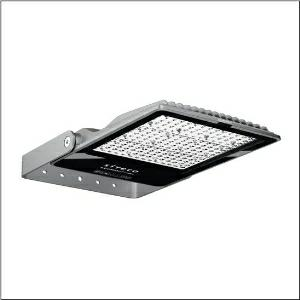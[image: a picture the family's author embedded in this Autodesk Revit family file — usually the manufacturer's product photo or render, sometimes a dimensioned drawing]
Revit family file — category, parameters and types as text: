
# Revit family: sicompact_r__31_midi___pl32_5xa7581e2k23_2195
name_source: partatom
category: Lighting Fixtures
units: mm (PartAtom-declared; Revit-internal decimal feet)

## family parameters
Cut with Voids When Loaded = No
Host = Face
Light Source = No
Part Type = Normal
Room Calculation Point = No
Round Connector Dimension = Use Diameter
Shared = No

## types (1)
- SiCompact® 31 midi  PL32 (1 x LED, 37000 lm, 243 W, 4000K)
    Apparent Load = 243 VA
    CIE Flux Codes = 32 69 98 100 100
    Color Rendering = 70
    Color Temperature = 4000K
    Default Elevation = 1800 mm
    Description = SiCompact® 31 midi, floodlight, primary light control with lens, of plastic, of toughened safety glass, transparent, light distribution: PL32, light emission: direct distribution, primary light characteristic: asymmetric, installation type: surface-mounted, LED, High Power LED, rated luminous flux: 37.000lm, luminous efficacy: 152lm/W, light colour: 740, colour temperature: 4000K, control gear: ON/OFF, with cable, 3x 1.5mm², mains connection: 220..240V, AC, 50/60Hz, connection cable pre-assembled, cable length: 2m, rated input power: 243W, of diecast aluminium, specular, metallic grey (RAL 9006), length: 560mm, width: 330mm, height: 62mm, bracket, of sheet steel, coated, metallic grey (RAL 9006), ON/OFF, protection rating (complete): IP66, insulation class (complete): insulation class I (protective earthing), certification: CE, ENEC, impact resistance: IK08, permissible operating ambient temperature: -40..+45°C, packaging unit: 1 piece

Light Distribution: PL32
    Height = 62 mm  [stored 0.203412 ft]
    Lamp = 1 x LED
    Lamp Light Flux = 37000 lm
    Lamp Power = 243 W
    Lamp count = 1
    Length = 560 mm
    Luminous efficacy = 152 lm/W
    Manufacturer = Siteco
    ModVariant = No
    Model = 5XA7581E2K23
    Mounting Place = Wall
    Mounting Type = Surface mounted
    Number of Poles = 1
    OnlyDefault = Yes
    Power Factor = 1
    Product Name = SiCompact® 31 midi | PL32
    Product group = floodlight | wall mounted
    ProductGroupID = 2001
    Protection Class = Protection class I
    Protection Degree = IP 66
    RLX_Detail_Level = 1
    RLX_Emergency_Light_Flux = 0 lm
    RLX_Emergency_Type = 0
    RLX_Emergency_Type_DB = No
    RlxData = <blob elided: 98189 chars, md5=66c6e39e>
    Socket = socket
    Standby Power = 0 W
    System Light Flux = 37000 lm
    System Power = 243 W
    Type Comments = Product without accessories
    Type Image = l_1006415.jpg
    URL = http://relux.com
    VarID = ---
    Voltage = 0 V
    Weight = 0.00 kg
    Width = 333 mm

note: [stored X ft] marks values corroborated as IEEE doubles in the binary element streams (Revit-internal decimal feet)

## geometry (parser evidence)
native form markers: Blend x4, Sweep x12
no freeform markers — native parametric forms only
